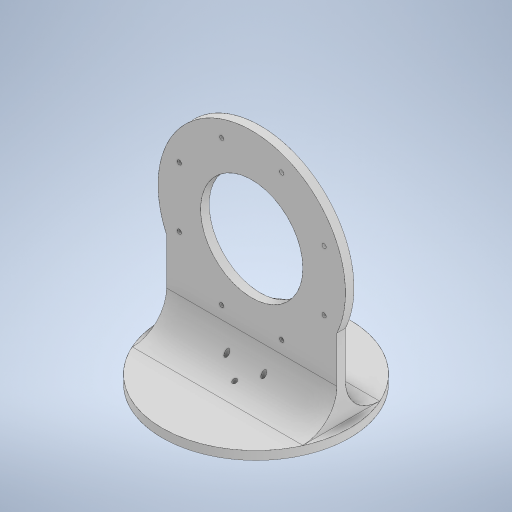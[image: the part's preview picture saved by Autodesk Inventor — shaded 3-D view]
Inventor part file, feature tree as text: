
AUTODESK INVENTOR PART (.ipt)
format: ipt  version: 2024.3 (Build 283343000, 343)  size: 347,648 bytes
history: native  units: mm
features: sketch x6, extrude x4, hole x2, other x1, fillet x1
ambient origin geometry x8: Origin, YZ Plane, XZ Plane, XY Plane, X Axis, Y Axis, Z Axis, Center Point
bodies: Body1 (feature_tree)
feature tree (14):
  other  "ソリッド1"
  extrude  "押し出し1"  Depth=97.0mm
  hole  "穴1"  [1 undecoded]
  extrude  "押し出し2"  Depth=50.0mm
  extrude  "押し出し12"  Depth=50.0mm
  extrude  "押し出し14"  Depth=50.0mm
  fillet  "フィレット6"  Radius=50.0mm
  hole  "穴5"  [1 undecoded]
  sketch  "スケッチ1"
  sketch  "スケッチ2"
  sketch  "スケッチ3"
  sketch  "スケッチ16"
  sketch  "スケッチ19"
  sketch  "スケッチ20"
note: 2 required parameter values undecoded (feature->parameter linkage not recoverable at this tier; creation-order binding heuristic only, values carry confidence <= 0.55)
